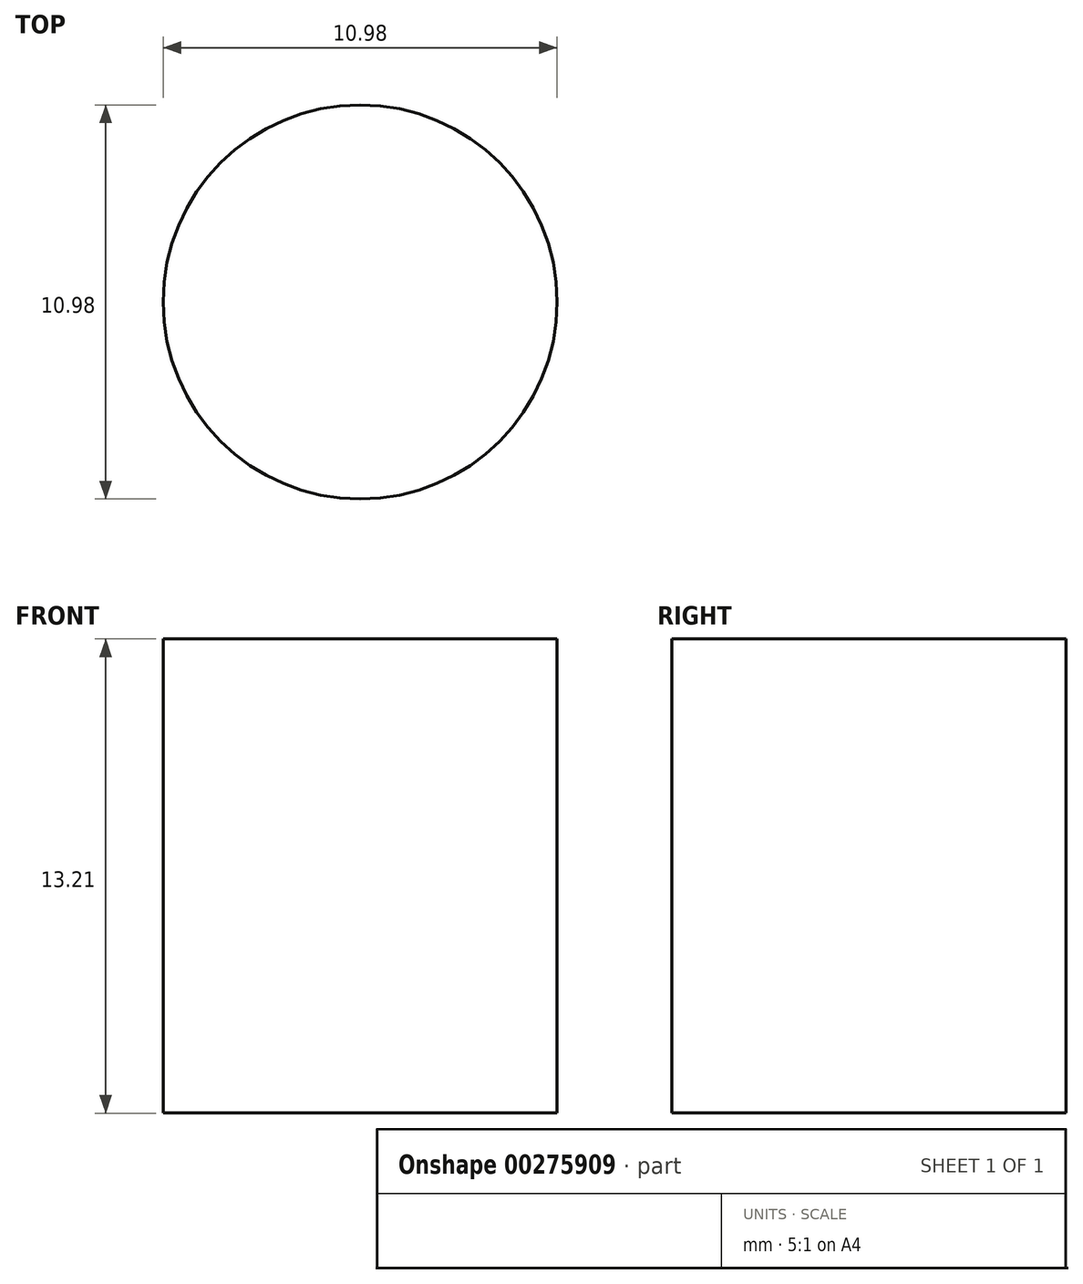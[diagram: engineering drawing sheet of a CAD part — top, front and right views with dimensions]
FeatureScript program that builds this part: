
annotation { "Feature Type Name" : "Feature", "Feature Type Description" : "" }
export const myFeature = defineFeature(function(context is Context, id is Id, definition is map)
    precondition{}
    {
        {
            var Q0;
            Q0=qCreatedBy(makeId("Top.planeOp"),FACE);
            var sketch = newSketch(context, id + "F0", { "sketchPlane" : qUnion([Q0])});
            skLineSegment(sketch, "E0.bottom", {"start": v(6.35, 6.35) * mm, "end": v(-6.35, 6.35) * mm});
            skLineSegment(sketch, "E0.top", {"start": v(6.35, -6.35) * mm, "end": v(-6.35, -6.35) * mm});
            skLineSegment(sketch, "E0.left", {"start": v(6.35, 6.35) * mm, "end": v(6.35, -6.35) * mm});
            skLineSegment(sketch, "E0.right", {"start": v(-6.35, 6.35) * mm, "end": v(-6.35, -6.35) * mm});
            skPoint(sketch, "E0.middle", {"position": v(0, 0) * mm});
            skCircle(sketch, "E1", {"center": v(0, 0) * mm, "radius": 5.5 * mm});
            skSolve(sketch);
        }
        {
            var Q0;
            Q0=makeQuery(id+"F0.imprint","IMPRINT",FACE,{"disambiguationData":[TD([[makeQuery(id+"F0.imprint","IMPRINT",EDGE,{"derivedFrom":sQuery(id+"F0.wireOp",EDGE,"E1")}),1.0]])]});
            extrude(context, id + "F1", {"entities" : qUnion([Q0]), "oppositeDirection" : true, "depth" : 13.2 * mm});
        }
    });
